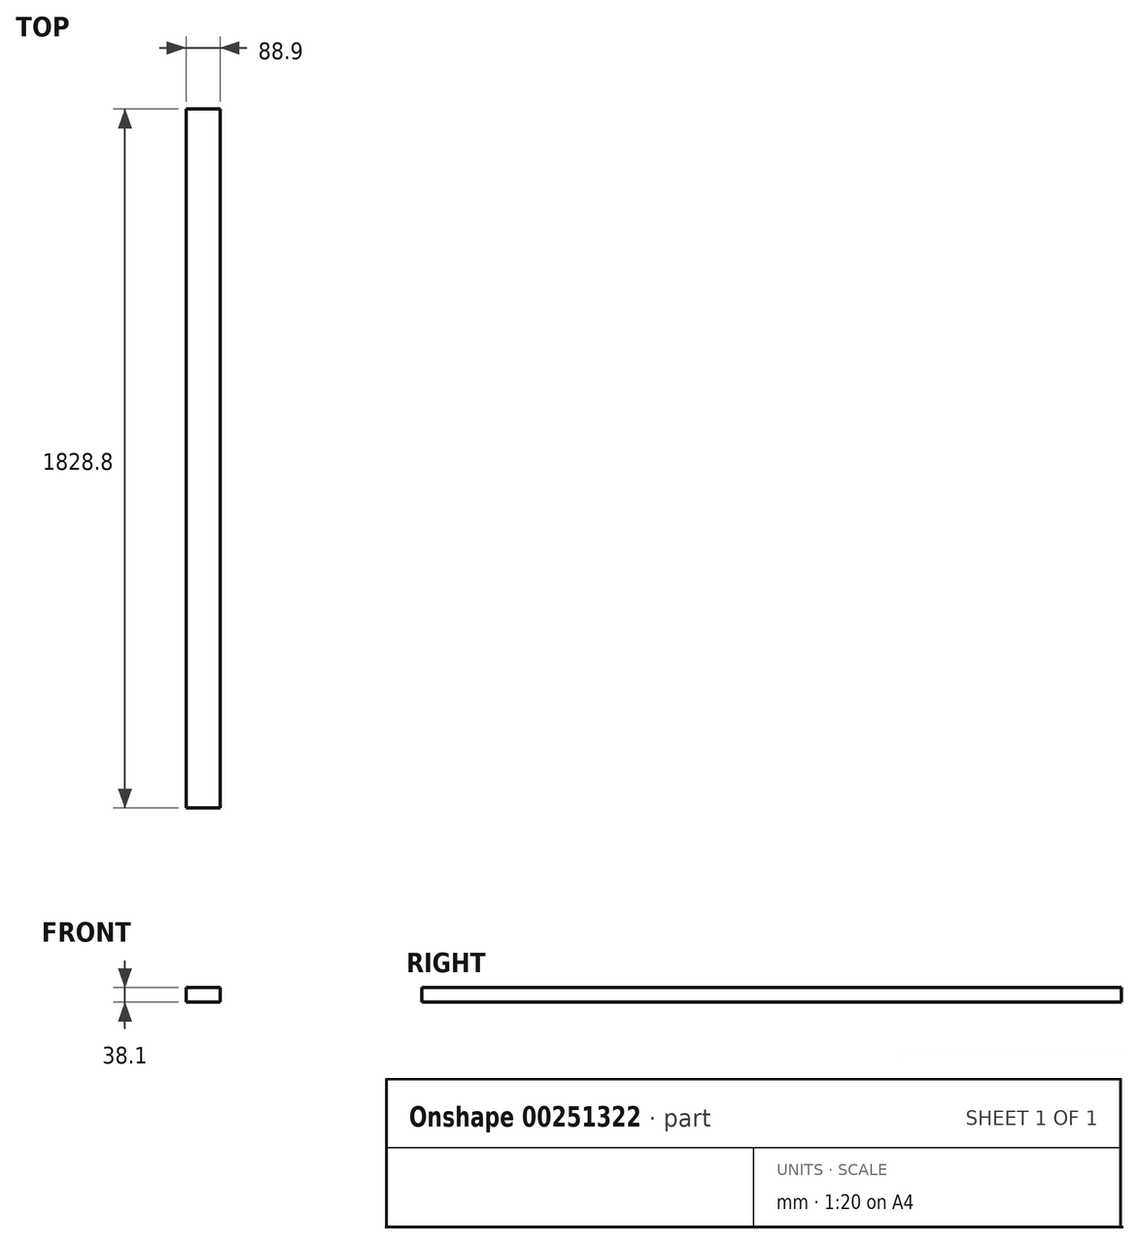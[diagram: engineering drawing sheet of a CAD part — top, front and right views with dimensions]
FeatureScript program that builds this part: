
annotation { "Feature Type Name" : "Feature", "Feature Type Description" : "" }
export const myFeature = defineFeature(function(context is Context, id is Id, definition is map)
    precondition{}
    {
        {
            var Q0;
            Q0=qCreatedBy(makeId("Top.planeOp"),FACE);
            var sketch = newSketch(context, id + "F0", { "sketchPlane" : qUnion([Q0])});
            skLineSegment(sketch, "E0.bottom", {"start": v(-75.42, 1286.56) * mm, "end": v(13.48, 1286.56) * mm});
            skLineSegment(sketch, "E0.top", {"start": v(-75.42, -542.24) * mm, "end": v(13.48, -542.24) * mm});
            skLineSegment(sketch, "E0.left", {"start": v(-75.42, 1286.56) * mm, "end": v(-75.42, -542.24) * mm});
            skLineSegment(sketch, "E0.right", {"start": v(13.48, 1286.56) * mm, "end": v(13.48, -542.24) * mm});
            skSolve(sketch);
        }
        {
            var Q0;
            Q0=makeQuery(id+"F0.imprint","IMPRINT",FACE,{"disambiguationData":[TD([[makeQuery(id+"F0.imprint","IMPRINT",EDGE,{"derivedFrom":sQuery(id+"F0.wireOp",EDGE,"E0.bottom")}),-1.0]])]});
            extrude(context, id + "F1", {"entities" : qUnion([Q0]), "depth" : 38.1 * mm});
        }
    });
